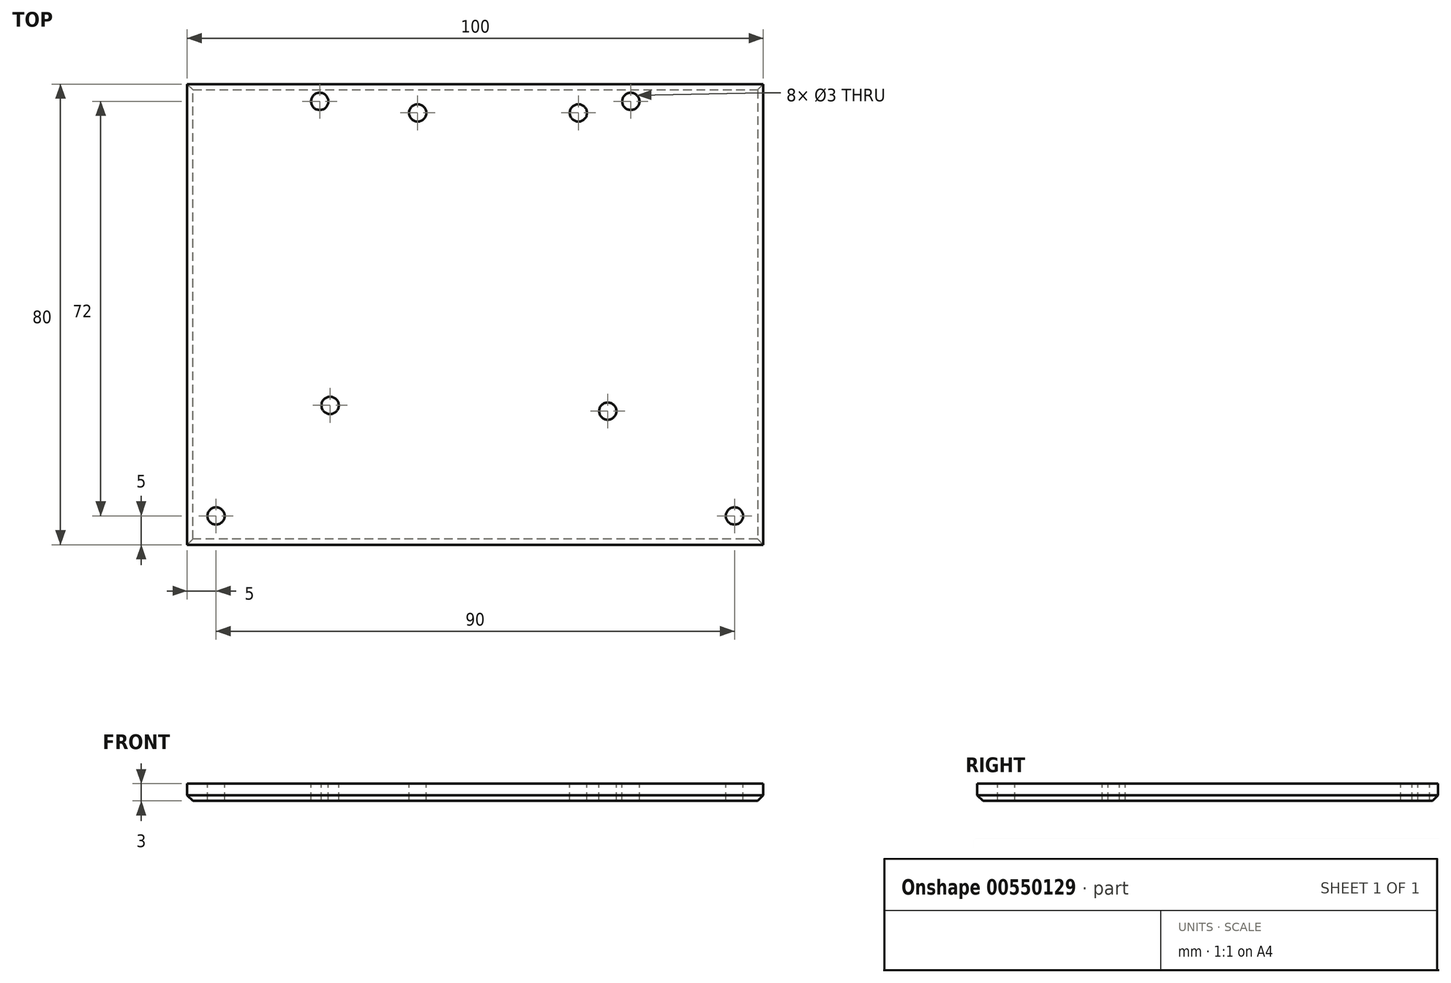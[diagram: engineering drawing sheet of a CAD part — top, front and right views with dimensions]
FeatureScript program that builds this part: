
annotation { "Feature Type Name" : "Feature", "Feature Type Description" : "" }
export const myFeature = defineFeature(function(context is Context, id is Id, definition is map)
    precondition{}
    {
        {
            var Q0;
            Q0=qCreatedBy(makeId("Top.planeOp"),FACE);
            var sketch = newSketch(context, id + "F0", { "sketchPlane" : qUnion([Q0])});
            skLineSegment(sketch, "E0.bottom", {"start": v(50, -40) * mm, "end": v(-50, -40) * mm});
            skLineSegment(sketch, "E0.top", {"start": v(50, 40) * mm, "end": v(-50, 40) * mm});
            skLineSegment(sketch, "E0.left", {"start": v(50, -40) * mm, "end": v(50, 40) * mm});
            skLineSegment(sketch, "E0.right", {"start": v(-50, -40) * mm, "end": v(-50, 40) * mm});
            skPoint(sketch, "E0.middle", {"position": v(0, 0) * mm});
            skSolve(sketch);
        }
        {
            var Q0;
            Q0=makeQuery(id+"F0.imprint","IMPRINT",FACE,{"disambiguationData":[TD([[makeQuery(id+"F0.imprint","IMPRINT",EDGE,{"derivedFrom":sQuery(id+"F0.wireOp",EDGE,"E0.bottom")}),-1.0]])]});
            extrude(context, id + "F1", {"entities" : qUnion([Q0]), "depth" : 3 * mm, "offsetDistance" : 25 * mm});
        }
        {
            var Q0;
            Q0=makeQuery(id+"F1.opExtrude","CAP_FACE",FACE,{"disambiguationData":[OSD([sQuery(id+"F0.wireOp",EDGE,"E0.bottom"),sQuery(id+"F0.wireOp",EDGE,"E0.top"),sQuery(id+"F0.wireOp",EDGE,"E0.left"),sQuery(id+"F0.wireOp",EDGE,"E0.right")])],"isStart":false});
            var sketch = newSketch(context, id + "F2", { "sketchPlane" : qUnion([Q0])});
            skLineSegment(sketch, "E1", {"start": v(0, 40) * mm, "end": v(0, -40) * mm});
            skLineSegment(sketch, "E2", {"start": v(-10, 40) * mm, "end": v(-10, -40) * mm});
            skLineSegment(sketch, "E3", {"start": v(-50, 35) * mm, "end": v(50, 35) * mm});
            skPoint(sketch, "E4", {"position": v(-10, 35) * mm});
            skLineSegment(sketch, "E5", {"start": v(17.9, 40) * mm, "end": v(17.9, -40) * mm});
            skPoint(sketch, "E6", {"position": v(17.9, 35) * mm});
            skLineSegment(sketch, "E7", {"start": v(-25.2, 35) * mm, "end": v(-25.2, -15.8) * mm});
            skPoint(sketch, "E8", {"position": v(-25.2, -15.8) * mm});
            skLineSegment(sketch, "E9", {"start": v(23, 35) * mm, "end": v(23, -16.8) * mm});
            skPoint(sketch, "E10", {"position": v(23, -16.8) * mm});
            skSolve(sketch);
        }
        {
            var Q0;
            Q0=sQuery(id+"F2.wireOp",VERTEX,"E4");
            var Q1;
            Q1=sQuery(id+"F2.wireOp",VERTEX,"E6");
            var Q2;
            Q2=sQuery(id+"F2.wireOp",VERTEX,"E10");
            var Q3;
            Q3=sQuery(id+"F2.wireOp",VERTEX,"E8");
            var Q4;
            Q4=makeQuery(id+"F1.opExtrude","SWEPT_BODY",BODY,{"disambiguationData":[OSD([sQuery(id+"F0.wireOp",EDGE,"E0.bottom"),sQuery(id+"F0.wireOp",EDGE,"E0.top"),sQuery(id+"F0.wireOp",EDGE,"E0.left"),sQuery(id+"F0.wireOp",EDGE,"E0.right")])]});
            hole(context, id + "F3", {"style" : HoleStyle.SIMPLE, "endStyle" : HoleEndStyle.THROUGH, "holeDiameter" : 3 * mm, "isTappedThrough" : true, "tappedDepth" : 12 * mm, "tapClearance" : 3, "locations" : qUnion([Q0, Q1, Q2, Q3]), "scope" : qUnion([Q4])});
        }
        {
            var Q0;
            Q0=makeQuery(id+"F1.opExtrude","CAP_EDGE",EDGE,{"disambiguationData":[OSD([sQuery(id+"F0.wireOp",EDGE,"E0.bottom")])],"isStart":true});
            var Q1;
            Q1=makeQuery(id+"F1.opExtrude","CAP_EDGE",EDGE,{"disambiguationData":[OSD([sQuery(id+"F0.wireOp",EDGE,"E0.right")])],"isStart":true});
            var Q2;
            Q2=makeQuery(id+"F1.opExtrude","CAP_EDGE",EDGE,{"disambiguationData":[OSD([sQuery(id+"F0.wireOp",EDGE,"E0.left")])],"isStart":true});
            var Q3;
            Q3=makeQuery(id+"F1.opExtrude","CAP_EDGE",EDGE,{"disambiguationData":[OSD([sQuery(id+"F0.wireOp",EDGE,"E0.top")])],"isStart":true});
            chamfer(context, id + "F4", {"entities" : qUnion([Q0, Q1, Q2, Q3]), "width" : 1 * mm, "tangentPropagation" : true});
        }
        {
            var Q0;
            Q0=makeQuery(id+"F1.opExtrude","CAP_FACE",FACE,{"disambiguationData":[OSD([sQuery(id+"F0.wireOp",EDGE,"E0.bottom"),sQuery(id+"F0.wireOp",EDGE,"E0.top"),sQuery(id+"F0.wireOp",EDGE,"E0.left"),sQuery(id+"F0.wireOp",EDGE,"E0.right")])],"isStart":false});
            var sketch = newSketch(context, id + "F5", { "sketchPlane" : qUnion([Q0])});
            skLineSegment(sketch, "E11", {"start": v(-45, 40) * mm, "end": v(-45, -40) * mm});
            skLineSegment(sketch, "E12", {"start": v(-50, -35) * mm, "end": v(50, -35) * mm});
            skLineSegment(sketch, "E13", {"start": v(45, 40) * mm, "end": v(45, -40) * mm});
            skPoint(sketch, "E14", {"position": v(-45, -35) * mm});
            skPoint(sketch, "E15", {"position": v(45, -35) * mm});
            skLineSegment(sketch, "E16", {"start": v(-27, 40) * mm, "end": v(-27, -40) * mm});
            skLineSegment(sketch, "E17", {"start": v(27, 40) * mm, "end": v(27, -40) * mm});
            skLineSegment(sketch, "E18", {"start": v(-50, 37) * mm, "end": v(50, 37) * mm});
            skPoint(sketch, "E19", {"position": v(-27, 37) * mm});
            skPoint(sketch, "E20", {"position": v(27, 37) * mm});
            skSolve(sketch);
        }
        {
            var Q0;
            Q0=sQuery(id+"F5.wireOp",VERTEX,"E14");
            var Q1;
            Q1=sQuery(id+"F5.wireOp",VERTEX,"E19");
            var Q2;
            Q2=sQuery(id+"F5.wireOp",VERTEX,"E20");
            var Q3;
            Q3=sQuery(id+"F5.wireOp",VERTEX,"E15");
            var Q4;
            Q4=makeQuery(id+"F1.opExtrude","SWEPT_BODY",BODY,{"disambiguationData":[OSD([sQuery(id+"F0.wireOp",EDGE,"E0.bottom"),sQuery(id+"F0.wireOp",EDGE,"E0.top"),sQuery(id+"F0.wireOp",EDGE,"E0.left"),sQuery(id+"F0.wireOp",EDGE,"E0.right")])]});
            hole(context, id + "F6", {"style" : HoleStyle.SIMPLE, "endStyle" : HoleEndStyle.THROUGH, "holeDiameter" : 3 * mm, "isTappedThrough" : true, "tappedDepth" : 12 * mm, "tapClearance" : 3, "locations" : qUnion([Q0, Q1, Q2, Q3]), "scope" : qUnion([Q4])});
        }
    });
